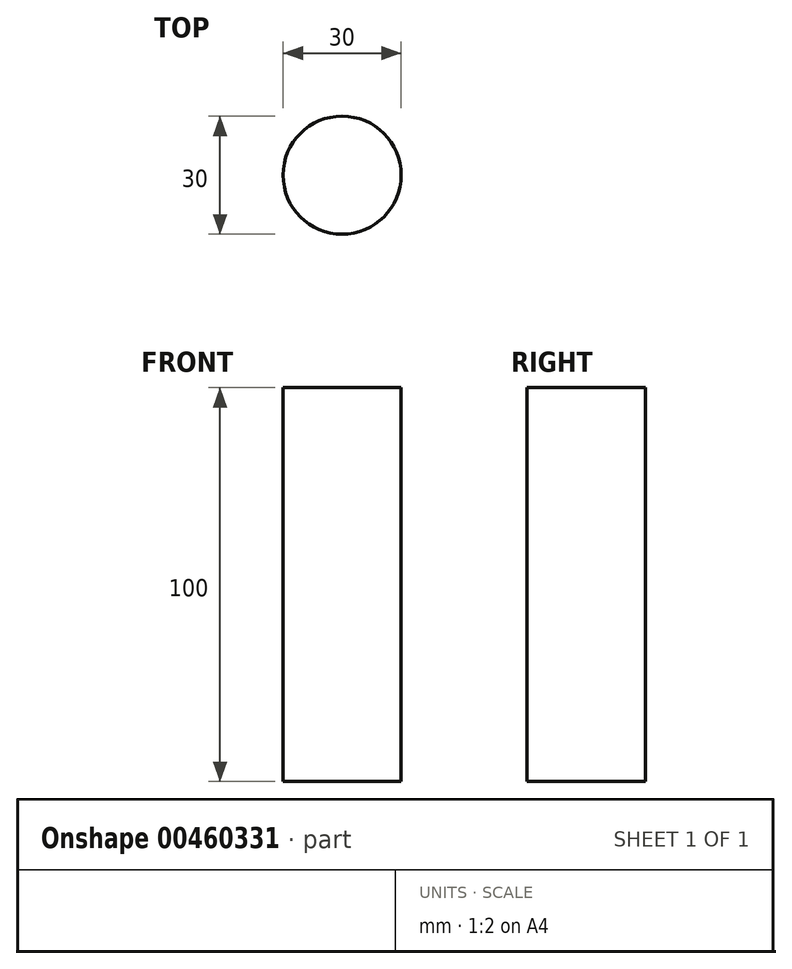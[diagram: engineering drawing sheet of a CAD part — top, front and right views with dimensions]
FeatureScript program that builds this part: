
annotation { "Feature Type Name" : "Feature", "Feature Type Description" : "" }
export const myFeature = defineFeature(function(context is Context, id is Id, definition is map)
    precondition{}
    {
        {
            var Q0;
            Q0=qCreatedBy(makeId("Top.planeOp"),FACE);
            var sketch = newSketch(context, id + "F0", { "sketchPlane" : qUnion([Q0])});
            skCircle(sketch, "E0", {"center": v(0, 0) * mm, "radius": 15 * mm});
            skSolve(sketch);
        }
        {
            var Q0;
            Q0 = qSketchRegion(id + "F0", true);
            extrude(context, id + "F1", {"entities" : qUnion([Q0]), "depth" : 100 * mm});
        }
    });
